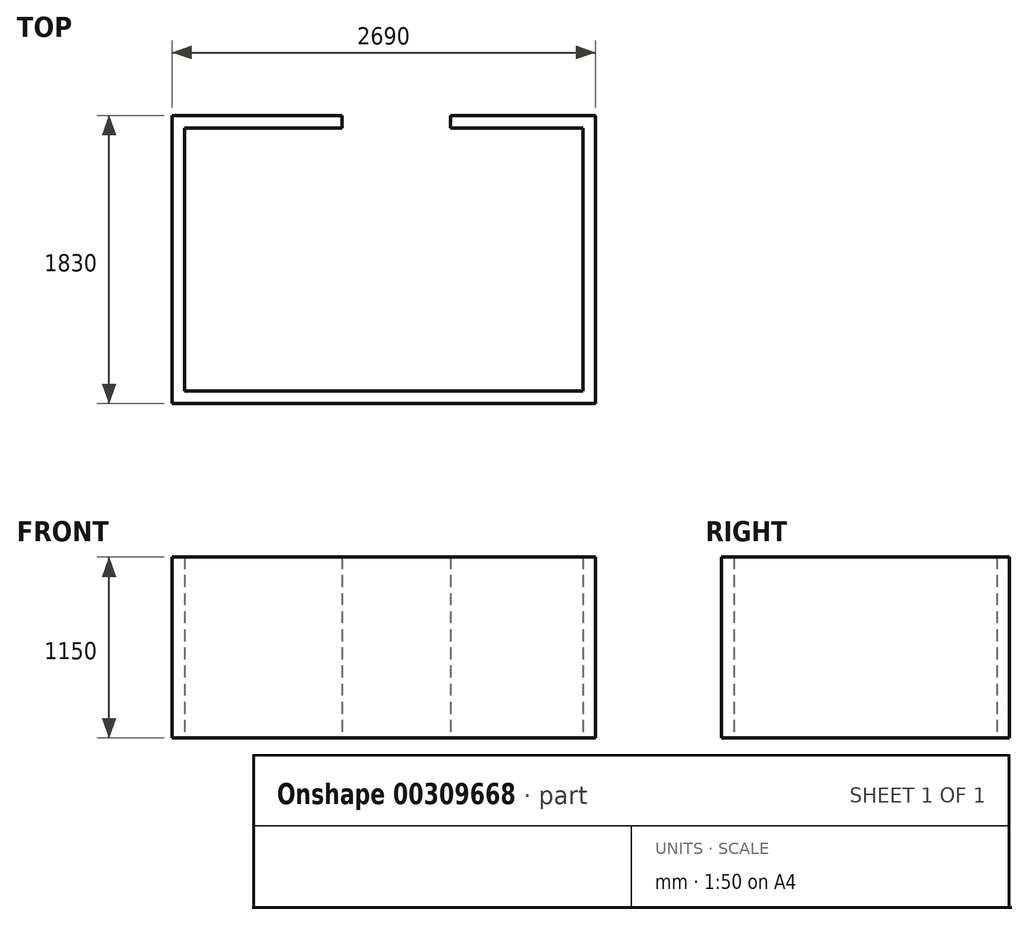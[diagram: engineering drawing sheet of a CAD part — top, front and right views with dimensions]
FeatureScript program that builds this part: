
annotation { "Feature Type Name" : "Feature", "Feature Type Description" : "" }
export const myFeature = defineFeature(function(context is Context, id is Id, definition is map)
    precondition{}
    {
        {
            var Q0;
            Q0=qCreatedBy(makeId("Top.planeOp"),FACE);
            var sketch = newSketch(context, id + "F0", { "sketchPlane" : qUnion([Q0])});
            skLineSegment(sketch, "E0.bottom", {"start": v(-1265, 835) * mm, "end": v(1265, 835) * mm});
            skLineSegment(sketch, "E0.top", {"start": v(-1265, -835) * mm, "end": v(1265, -835) * mm});
            skLineSegment(sketch, "E0.left", {"start": v(-1265, 835) * mm, "end": v(-1265, -835) * mm});
            skLineSegment(sketch, "E0.right", {"start": v(1265, 835) * mm, "end": v(1265, -835) * mm});
            skLineSegment(sketch, "E1", {"start": v(0, 0) * mm, "end": v(0, 835) * mm, "construction": true});
            skLineSegment(sketch, "E2", {"start": v(0, 0) * mm, "end": v(1265, 0) * mm, "construction": true});
            skLineSegment(sketch, "E3", {"start": v(-415, 195) * mm, "end": v(-415, 835) * mm});
            skLineSegment(sketch, "E4", {"start": v(-1265, 195) * mm, "end": v(-415, 195) * mm, "construction": true});
            skLineSegment(sketch, "E5.bottom", {"start": v(215, -835) * mm, "end": v(540, -835) * mm});
            skLineSegment(sketch, "E5.top", {"start": v(215, -565) * mm, "end": v(540, -565) * mm});
            skLineSegment(sketch, "E5.left", {"start": v(215, -835) * mm, "end": v(215, -565) * mm});
            skLineSegment(sketch, "E5.right", {"start": v(540, -835) * mm, "end": v(540, -565) * mm});
            skLineSegment(sketch, "E6", {"start": v(-105, -835) * mm, "end": v(-105, -411.19) * mm, "construction": true});
            skLineSegment(sketch, "E7", {"start": v(-1265, 435) * mm, "end": v(-415, 435) * mm});
            skLineSegment(sketch, "E8.bottom", {"start": v(-335, 835) * mm, "end": v(-265, 835) * mm});
            skLineSegment(sketch, "E8.top", {"start": v(-335, 815) * mm, "end": v(-265, 815) * mm});
            skLineSegment(sketch, "E8.left", {"start": v(-335, 835) * mm, "end": v(-335, 815) * mm});
            skLineSegment(sketch, "E8.right", {"start": v(-265, 835) * mm, "end": v(-265, 815) * mm});
            skLineSegment(sketch, "E9.bottom", {"start": v(425, 835) * mm, "end": v(495, 835) * mm});
            skLineSegment(sketch, "E9.top", {"start": v(425, 815) * mm, "end": v(495, 815) * mm});
            skLineSegment(sketch, "E9.left", {"start": v(425, 835) * mm, "end": v(425, 815) * mm});
            skLineSegment(sketch, "E9.right", {"start": v(495, 835) * mm, "end": v(495, 815) * mm});
            skLineSegment(sketch, "E10", {"start": v(-265, 835) * mm, "end": v(-265, 915) * mm});
            skLineSegment(sketch, "E11", {"start": v(-265, 915) * mm, "end": v(-1345, 915) * mm});
            skLineSegment(sketch, "E12", {"start": v(-1345, 915) * mm, "end": v(-1345, -915) * mm});
            skLineSegment(sketch, "E13", {"start": v(-1345, -915) * mm, "end": v(1345, -915) * mm});
            skLineSegment(sketch, "E14", {"start": v(1345, -915) * mm, "end": v(1345, 915) * mm});
            skLineSegment(sketch, "E15", {"start": v(1345, 915) * mm, "end": v(425, 915) * mm});
            skLineSegment(sketch, "E16", {"start": v(425, 915) * mm, "end": v(425, 835) * mm});
            skLineSegment(sketch, "E17", {"start": v(-1265, 835) * mm, "end": v(-1345, 835) * mm, "construction": true});
            skLineSegment(sketch, "E18", {"start": v(1265, 835) * mm, "end": v(1345, 835) * mm, "construction": true});
            skLineSegment(sketch, "E19", {"start": v(-1265, -835) * mm, "end": v(-1265, -915) * mm, "construction": true});
            skSolve(sketch);
        }
        {
            var Q0;
            {var subQ1=sQuery(id+"F0.wireOp",EDGE,"E0.right");Q0=makeQuery(id+"F0.imprint","IMPRINT",FACE,{"disambiguationData":[TD([[makeQuery(id+"F0.imprint","IMPRINT",EDGE,{"derivedFrom":subQ1}),1.0]])]});}
            var Q1;
            Q1=makeQuery(id+"F0.imprint","IMPRINT",FACE,{"disambiguationData":[TD([[makeQuery(id+"F0.imprint","IMPRINT",EDGE,{"derivedFrom":sQuery(id+"F0.wireOp",EDGE,"E5.bottom")}),1.0]])]});
            extrude(context, id + "F1", {"entities" : qUnion([Q0, Q1]), "depth" : 1150 * mm});
        }
    });
